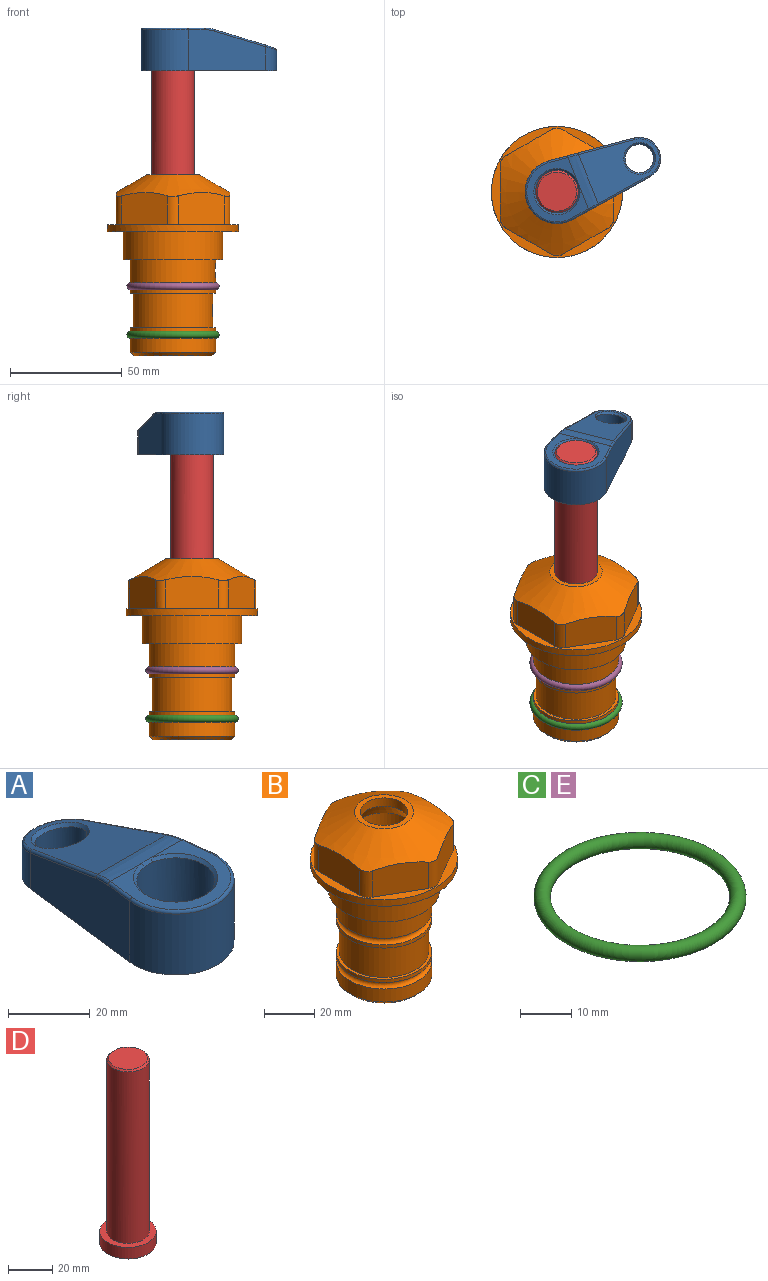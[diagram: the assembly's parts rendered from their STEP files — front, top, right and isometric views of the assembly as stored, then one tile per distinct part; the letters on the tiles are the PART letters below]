
ASSEMBLY  parts=5 mates=4
PART A: 31 faces, bbox 31.7x65.5x19.8 mm
  f0: plane 39.12x18.26mm, normal (0.99,0.12,0), area 612.2mm2, adj f1,f4,f7,f11,f13,f15
  f1: cylinder r=9.53mm len=18.91mm, axis (0,0,-1), area 296.1mm2, adj f0,f2,f7,f17
  f2: plane 39.12x18.26mm, normal (-0.99,0.12,0), area 612.2mm2, adj f1,f4,f7,f12,f14,f16
  f3: cylinder r=6.35mm len=12.7mm, axis (0,0,-1), area 362.4mm2, adj f7,f18
  f4: cylinder r=14.29mm len=28.58mm, axis (0,0,-1), area 882.2mm2, adj f0,f2,f7,f10
  f5: cylinder r=9.53mm len=19.05mm, axis (0,0,-1), area 1092.6mm2, adj f7,f19,f20
  f6: plane 26.99x23.69mm, normal (0,0,1), area 216.2mm2, adj f9,f10,f11,f12,f19
  f7: plane 63.5x28.58mm, normal (0,0,-1), area 661.8mm2, adj f0,f1,f2,f3,f4,f5,f22,f23
  f8: plane 33.52x23.6mm, normal (0,0.26,0.97), area 486mm2, adj f9,f15,f16,f17,f18
  f9: cylinder r=19.05mm len=24.72mm, axis (1,0,0), area 120.4mm2, adj f6,f8,f13,f14,f20
  f10: torus R=13.49mm, axis (0,0,1), area 59mm2, adj f4,f6,f11,f12
  f11: cylinder r=0.79mm len=8.67mm, axis (0.12,-0.99,0), area 10.8mm2, adj f0,f6,f10,f13
  f12: cylinder r=0.79mm len=8.67mm, axis (0.12,0.99,0), area 10.8mm2, adj f2,f6,f10,f14
  f13: bspline ~4.95x1.42mm, area 6.1mm2, adj f0,f9,f11,f15
  f14: bspline ~4.95x1.42mm, area 6.1mm2, adj f2,f9,f12,f16
  f15: cylinder r=0.79mm len=25.95mm, axis (0.12,-0.96,0.26), area 32.9mm2, adj f0,f8,f13,f17
  f16: cylinder r=0.79mm len=25.95mm, axis (0.12,0.96,-0.26), area 32.9mm2, adj f2,f8,f14,f17
  f17: bspline ~18.91x8.38mm, area 30mm2, adj f1,f8,f15,f16
  f18: bspline ~14.29x14.29mm, area 48.3mm2, adj f3,f8
  f19: cone r=9.53mm half-angle=45deg, axis (0,0,1), area 66.5mm2, adj f5,f6,f20
  f20: bspline ~3.22x0.96mm, area 3.5mm2, adj f5,f9,f19
  f21: plane 2.75x2.72mm, normal (0,0,-1), area 2.9mm2, adj f23,f25,f28
  f22: plane 23.05x15.88mm, normal (-0.99,-0.12,0), area 323.6mm2, adj f7,f25,f26,f27,f28,f29
  f23: plane 23.05x15.88mm, normal (0.99,-0.12,0), area 323.6mm2, adj f7,f21,f25,f27,f28,f30
  f24: cylinder r=9.53mm len=10.69mm, axis (0,0,-1), area 114.7mm2, adj f7,f27,f29,f30
  f25: cylinder r=12.7mm len=20.59mm, axis (0,0,-1), area 381.1mm2, adj f7,f21,f22,f23,f26,f28
  f26: plane 2.75x2.72mm, normal (0,0,-1), area 2.9mm2, adj f22,f25,f28
  f27: plane 19.72x18.37mm, normal (0,-0.26,-0.97), area 291.8mm2, adj f22,f23,f24,f28,f29,f30
  f28: cylinder r=15.88mm len=19.92mm, axis (1,0,0), area 54.8mm2, adj f21,f22,f23,f25,f26,f27
  f29: cylinder r=1.59mm len=11mm, axis (0,0,-1), area 34.7mm2, adj f7,f22,f24,f27
  f30: cylinder r=1.59mm len=11mm, axis (0,0,-1), area 34.7mm2, adj f7,f23,f24,f27
PART B: 36 faces, bbox 58.7x58.7x81 mm
  f0: cylinder r=17.78mm len=35.56mm, axis (0,0,1), area 1670.8mm2, adj f23,f24,f31
  f1: cylinder r=19.05mm len=38.1mm, axis (0,0,1), area 1191.9mm2, adj f26,f27,f30
  f2: plane 58.66x58.66mm, normal (0,0,-1), area 1150.6mm2, adj f3,f28
  f3: cylinder r=29.33mm len=58.66mm, axis (0,0,-1), area 585.1mm2, adj f2,f4
  f4: plane 58.66x58.66mm, normal (0,0,1), area 475.9mm2, adj f3,f5,f6,f7,f8,f9,f10,f11
  f5: plane 20.32x14.34mm, normal (-0.5,0.87,0), area 324.4mm2, adj f4,f15,f16,f17
  f6: plane 20.32x14.34mm, normal (0.5,0.87,0), area 324.4mm2, adj f4,f14,f15,f17
  f7: plane 23.48x14.34mm, normal (1,0,0), area 324.4mm2, adj f4,f13,f14,f17
  f8: plane 20.32x14.34mm, normal (0.5,-0.87,0), area 324.4mm2, adj f4,f12,f13,f17
  f9: plane 20.32x14.34mm, normal (-0.5,-0.87,0), area 324.4mm2, adj f4,f11,f12,f17
  f10: plane 23.48x14.34mm, normal (-1,0,0), area 324.4mm2, adj f4,f11,f16,f17
  f11: cylinder r=5.08mm len=12.85mm, axis (0,0,-1), area 67.2mm2, adj f4,f9,f10,f17
  f12: cylinder r=5.08mm len=12.85mm, axis (0,0,-1), area 67.2mm2, adj f4,f8,f9,f17
  f13: cylinder r=5.08mm len=12.85mm, axis (0,0,-1), area 67.2mm2, adj f4,f7,f8,f17
  f14: cylinder r=5.08mm len=12.85mm, axis (0,0,-1), area 67.2mm2, adj f4,f6,f7,f17
  f15: cylinder r=5.08mm len=12.85mm, axis (0,0,-1), area 67.2mm2, adj f4,f5,f6,f17
  f16: cylinder r=5.08mm len=12.85mm, axis (0,0,-1), area 67.2mm2, adj f4,f5,f10,f17
  f17: cone r=11.73mm half-angle=60deg, axis (0,0,-1), area 2071.8mm2, adj f5,f6,f7,f8,f9,f10,f11,f12
  f18: plane 23.46x23.46mm, normal (0,0,1), area 147.4mm2, adj f17,f35
  f19: plane 34.93x34.93mm, normal (0,0,-1), area 958mm2, adj f29
  f20: cylinder r=19.05mm len=38.1mm, axis (0,0,1), area 760.1mm2, adj f21,f29
  f21: torus R=19.05mm, axis (0,0,1), area 565.3mm2, adj f20,f22
  f22: cylinder r=19.05mm len=38.1mm, axis (0,0,1), area 190mm2, adj f21,f23
  f23: plane 38.1x38.1mm, normal (0,0,1), area 146.9mm2, adj f0,f22
  f24: plane 38.1x38.1mm, normal (0,0,-1), area 146.9mm2, adj f0,f25
  f25: cylinder r=19.05mm len=38.1mm, axis (0,0,1), area 190mm2, adj f24,f26
  f26: torus R=19.05mm, axis (0,0,1), area 565.3mm2, adj f1,f25
  f27: plane 44.45x44.45mm, normal (0,0,-1), area 411.7mm2, adj f1,f28
  f28: cylinder r=22.23mm len=44.45mm, axis (0,0,1), area 1773.5mm2, adj f2,f27
  f29: cone r=19.05mm half-angle=45deg, axis (0,0,1), area 257.5mm2, adj f19,f20
  f30: cylinder r=3.17mm len=6.75mm, axis (-1,0,0), area 128mm2, adj f1,f33
  f31: cylinder r=3.17mm len=6.35mm, axis (-1,0,0), area 102.5mm2, adj f0,f33
  f32: plane 25.4x25.4mm, normal (0,0,1), area 506.7mm2, adj f33
  f33: cylinder r=12.7mm len=66.42mm, axis (0,0,-1), area 5236.2mm2, adj f30,f31,f32,f34
  f34: cone r=9.53mm half-angle=30deg, axis (0,0,-1), area 443.4mm2, adj f33,f35
  f35: cylinder r=9.53mm len=19.05mm, axis (0,0,-1), area 240.9mm2, adj f18,f34
PART C: 1 faces, bbox 44.7x44.7x3.2 mm
  f0: torus R=19.05mm, axis (0,0,1), area 1193.9mm2
PART D: 6 faces, bbox 25.4x25.4x101.6 mm
  f0: plane 17.46x17.46mm, normal (0,0,1), area 239.5mm2, adj f5
  f1: plane 25.4x25.4mm, normal (0,0,-1), area 506.7mm2, adj f2
  f2: cylinder r=12.7mm len=25.4mm, axis (0,0,1), area 506.7mm2, adj f1,f3
  f3: plane 25.4x25.4mm, normal (0,0,1), area 221.7mm2, adj f2,f4
  f4: cylinder r=9.53mm len=94.46mm, axis (0,0,1), area 5653mm2, adj f3,f5
  f5: cone r=8.73mm half-angle=45deg, axis (0,0,-1), area 64.4mm2, adj f0,f4
PART E: same geometry as C
PLACE A rot(axis=(0,0,-1),68.1deg) t=(0,0,27.55)mm
PLACE B at identity fixed
PLACE C t=(0,0,-21.59)mm
PLACE D rot(axis=(0,0,-1),68.1deg) t=(0,0,27.55)mm
PLACE E at identity
MATE cylindrical D.f2 <-> B.f0  axis (0,0,-1) through (0,0,-10.55)mm
MATE fastened D.f2 <-> A.f4  axis (0,0,-1) through (0,0,90.26)mm
MATE fastened E.f0 <-> B.f0  axis (0,0,1) through (0,0,-24.51)mm
MATE fastened C.f0 <-> B.f0  axis (0,0,1) through (0,0,-46.1)mm
